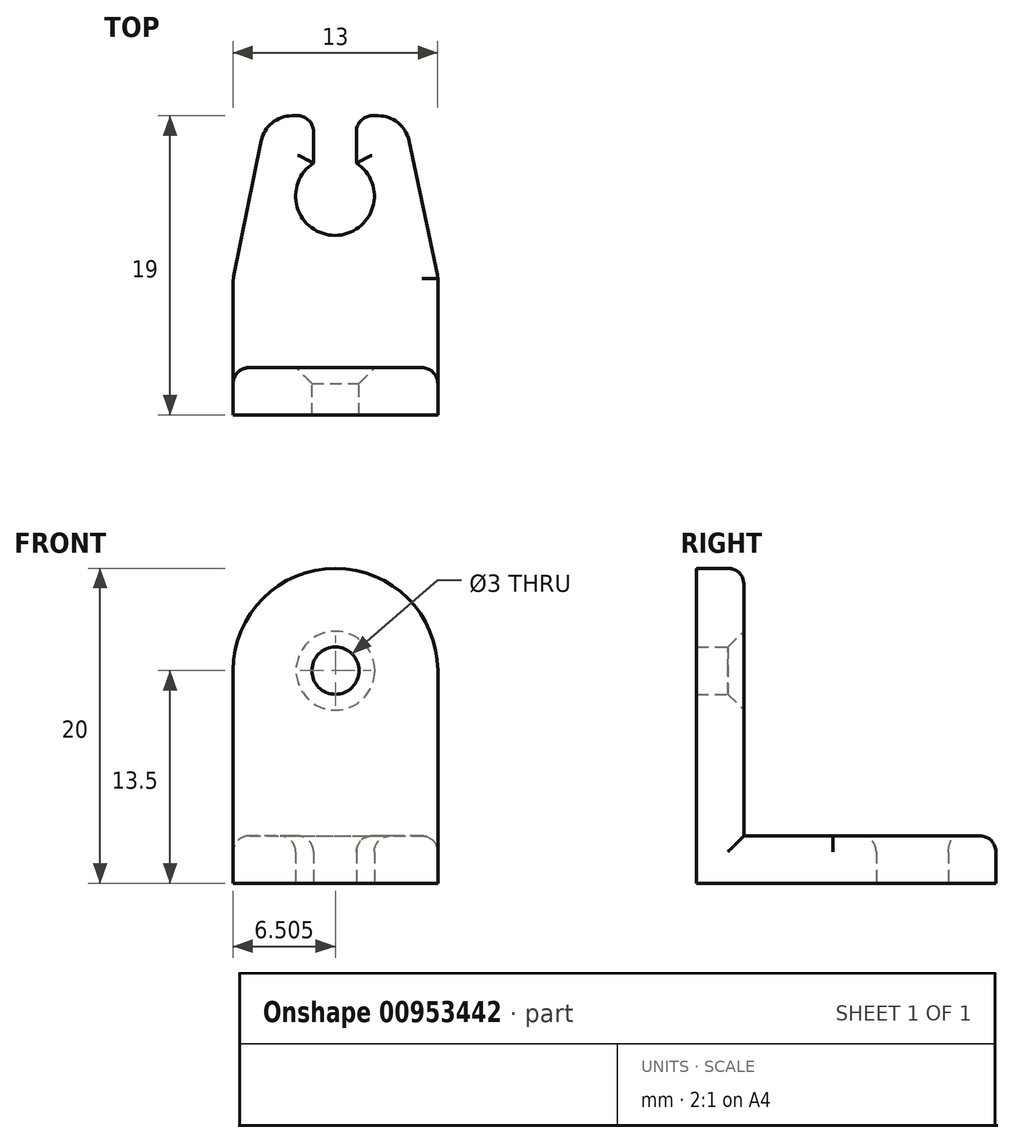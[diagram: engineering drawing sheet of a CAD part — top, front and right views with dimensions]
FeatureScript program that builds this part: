
annotation { "Feature Type Name" : "Feature", "Feature Type Description" : "" }
export const myFeature = defineFeature(function(context is Context, id is Id, definition is map)
    precondition{}
    {
        {
            var Q0;
            Q0=qCreatedBy(makeId("Top.planeOp"),FACE);
            var sketch = newSketch(context, id + "F0", { "sketchPlane" : qUnion([Q0])});
            skLineSegment(sketch, "E0", {"start": v(-22.66, 3.75) * mm, "end": v(-9.66, 3.75) * mm});
            skLineSegment(sketch, "E1", {"start": v(-9.66, 12.51) * mm, "end": v(-11.49, 21.16) * mm});
            skLineSegment(sketch, "E2", {"start": v(-13.44, 22.75) * mm, "end": v(-13.82, 22.75) * mm});
            skLineSegment(sketch, "E3", {"start": v(-14.82, 21.75) * mm, "end": v(-14.82, 19.75) * mm});
            skLineSegment(sketch, "E4", {"start": v(-17.55, 19.75) * mm, "end": v(-17.55, 21.75) * mm});
            skLineSegment(sketch, "E5", {"start": v(-18.55, 22.75) * mm, "end": v(-18.91, 22.75) * mm});
            skLineSegment(sketch, "E6", {"start": v(-20.87, 21.14) * mm, "end": v(-22.62, 12.53) * mm});
            skArc(sketch, "E7", {"start": v(-17.55, 19.75) * mm, "mid": v(-16.19, 15.15) * mm, "end": v(-14.82, 19.75) * mm});
            skPoint(sketch, "E7.third.point", {"position": v(-16.2, 15.15) * mm});
            skLineSegment(sketch, "E8.0", {"start": v(-22.66, 6.75) * mm, "end": v(-9.66, 6.75) * mm});
            skPoint(sketch, "E9.visualSharp", {"position": v(-20.55, 22.75) * mm});
            skArc(sketch, "E9.filletArc", {"start": v(-18.91, 22.75) * mm, "mid": v(-20.18, 22.3) * mm, "end": v(-20.87, 21.14) * mm});
            skPoint(sketch, "E10.visualSharp", {"position": v(-17.55, 22.75) * mm});
            skArc(sketch, "E10.filletArc", {"start": v(-17.55, 21.75) * mm, "mid": v(-17.84, 22.45) * mm, "end": v(-18.55, 22.75) * mm});
            skPoint(sketch, "E11.visualSharp", {"position": v(-11.82, 22.75) * mm});
            skArc(sketch, "E11.filletArc", {"start": v(-11.49, 21.16) * mm, "mid": v(-12.18, 22.3) * mm, "end": v(-13.44, 22.75) * mm});
            skPoint(sketch, "E12.visualSharp", {"position": v(-22.66, 12.33) * mm});
            skArc(sketch, "E12.filletArc", {"start": v(-22.62, 12.53) * mm, "mid": v(-22.65, 12.33) * mm, "end": v(-22.66, 12.13) * mm});
            skPoint(sketch, "E13.visualSharp", {"position": v(-14.82, 22.75) * mm});
            skArc(sketch, "E13.filletArc", {"start": v(-13.82, 22.75) * mm, "mid": v(-14.53, 22.45) * mm, "end": v(-14.82, 21.75) * mm});
            skLineSegment(sketch, "E14", {"start": v(-22.66, 3.75) * mm, "end": v(-22.66, 6.75) * mm});
            skLineSegment(sketch, "E15", {"start": v(-22.66, 12.13) * mm, "end": v(-22.66, 6.75) * mm});
            skLineSegment(sketch, "E16", {"start": v(-9.66, 12.51) * mm, "end": v(-9.66, 6.75) * mm});
            skLineSegment(sketch, "E17", {"start": v(-9.66, 3.75) * mm, "end": v(-9.66, 6.75) * mm});
            skLineSegment(sketch, "E18", {"start": v(-16.16, 6.75) * mm, "end": v(-16.16, 3.75) * mm});
            skSolve(sketch);
        }
        {
            var Q0;
            Q0=makeQuery(id+"F0.imprint","IMPRINT",FACE,{"disambiguationData":[TD([[makeQuery(id+"F0.imprint","IMPRINT",EDGE,{"derivedFrom":sQuery(id+"F0.wireOp",EDGE,"E0")}),1.0]])]});
            extrude(context, id + "F1", {"entities" : qUnion([Q0]), "depth" : 20 * mm, "offsetDistance" : 25 * mm});
        }
        {
            var Q0;
            Q0=makeQuery(id+"F0.imprint","IMPRINT",FACE,{"disambiguationData":[TD([[makeQuery(id+"F0.imprint","IMPRINT",EDGE,{"derivedFrom":sQuery(id+"F0.wireOp",EDGE,"E1")}),1.0]])]});
            extrude(context, id + "F2", {"entities" : qUnion([Q0]), "operationType" : NewBodyOperationType.ADD, "depth" : 3 * mm, "offsetDistance" : 25 * mm});
        }
        {
            var Q0;
            Q0=makeQuery(id+"F1.opExtrude","CAP_EDGE",EDGE,{"disambiguationData":[OSD([sQuery(id+"F0.wireOp",EDGE,"E17")])],"isStart":false});
            var Q1;
            Q1=makeQuery(id+"F1.opExtrude","CAP_EDGE",EDGE,{"disambiguationData":[OSD([sQuery(id+"F0.wireOp",EDGE,"E14")])],"isStart":false});
            fillet(context, id + "F3", {"entities" : qUnion([Q0, Q1]), "radius" : 6.5 * mm, "tangentPropagation" : true, "allowEdgeOverflow" : false});
        }
        {
            var Q0;
            Q0=makeQuery(id+"F1.opExtrude","SWEPT_EDGE",EDGE,{"disambiguationData":[OSD([sQuery(id+"F0.wireOp",EDGE,"E8.0"),sQuery(id+"F0.wireOp",EDGE,"E16"),sQuery(id+"F0.wireOp",EDGE,"E17")])]});
            fillet(context, id + "F4", {"entities" : qUnion([Q0]), "radius" : 1 * mm, "tangentPropagation" : true, "allowEdgeOverflow" : false});
        }
        {
            var Q0;
            Q0=makeQuery(id+"F2.opExtrude","CAP_EDGE",EDGE,{"disambiguationData":[OSD([sQuery(id+"F0.wireOp",EDGE,"E16")])],"isStart":false});
            fillet(context, id + "F5", {"entities" : qUnion([Q0]), "radius" : 1 * mm, "tangentPropagation" : true, "allowEdgeOverflow" : false});
        }
        {
            var Q0;
            Q0=makeQuery(id+"F2.opExtrude","CAP_EDGE",EDGE,{"disambiguationData":[OSD([sQuery(id+"F0.wireOp",EDGE,"E1")])],"isStart":false});
            var Q1;
            Q1=makeQuery(id+"F2.opExtrude","CAP_EDGE",EDGE,{"disambiguationData":[OSD([sQuery(id+"F0.wireOp",EDGE,"E9.filletArc")])],"isStart":false});
            var Q2;
            Q2=makeQuery(id+"F2.opExtrude","CAP_EDGE",EDGE,{"disambiguationData":[OSD([sQuery(id+"F0.wireOp",EDGE,"E7")])],"isStart":false});
            fillet(context, id + "F6", {"entities" : qUnion([Q0, Q1, Q2]), "radius" : 1 * mm, "tangentPropagation" : true, "allowEdgeOverflow" : false});
        }
        {
            var Q0;
            Q0=makeQuery(id+"F1.opExtrude","SWEPT_FACE",FACE,{"disambiguationData":[OSD([sQuery(id+"F0.wireOp",EDGE,"E8.0")])]});
            var sketch = newSketch(context, id + "F7", { "sketchPlane" : qUnion([Q0])});
            skLineSegment(sketch, "E19", {"start": v(10.66, 13.5) * mm, "end": v(21.66, 13.5) * mm});
            skLineSegment(sketch, "E20", {"start": v(16.16, 19) * mm, "end": v(16.16, 13.5) * mm});
            skCircle(sketch, "E21", {"center": v(16.16, 13.5) * mm, "radius": 1.5 * mm});
            skSolve(sketch);
        }
        {
            var Q0;
            Q0=sQuery(id+"F7.wireOp",VERTEX,"E20.end");
            var Q1;
            Q1=makeQuery(id+"F1.opExtrude","SWEPT_BODY",BODY,{"disambiguationData":[OSD([sQuery(id+"F0.wireOp",EDGE,"E0"),sQuery(id+"F0.wireOp",EDGE,"E8.0"),sQuery(id+"F0.wireOp",EDGE,"E14"),sQuery(id+"F0.wireOp",EDGE,"E17")])]});
            hole(context, id + "F8", {"style" : HoleStyle.C_SINK, "endStyle" : HoleEndStyle.THROUGH, "holeDiameter" : 3 * mm, "cSinkDiameter" : 5 * mm, "cSinkAngle" : 90 * degree, "majorDiameter" : 5 * mm, "isTappedThrough" : true, "tappedDepth" : 12 * mm, "tapClearance" : 3, "locations" : qUnion([Q0]), "scope" : qUnion([Q1])});
        }
    });
